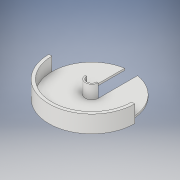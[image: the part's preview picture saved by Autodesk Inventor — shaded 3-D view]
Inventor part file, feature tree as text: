
AUTODESK INVENTOR PART (.ipt)
format: ipt  version: 2017 (Build 210142000, 142)  size: 180,736 bytes
history: native  units: in
note: dims shown in document units (in); Inventor stores cm internally (conversion verified against a paired STEP export)
features: sketch x10, extrude x9, projected_geometry x1
ambient origin geometry x8: Origin, YZ Plane, XZ Plane, XY Plane, X Axis, Y Axis, Z Axis, Center Point
bodies: Solid1 (feature_tree)
feature tree (20):
  extrude  "Extrusion1"  Depth=1.1024in TaperAngle=0.0deg
  extrude  "Extrusion2"  Depth=0.6496in TaperAngle=0.0deg
  extrude  "Extrusion3"  Depth=0.8268in
  extrude  "Extrusion4"  Depth=0.8661in TaperAngle=0.0deg
  extrude  "Extrusion5"  Depth=0.1181in TaperAngle=0.0deg
  extrude  "Extrusion6"  Depth=0.1181in TaperAngle=0.0deg
  sketch  "Sketch7"  dims[d22=0.1181in d23=0.0in]
  extrude  "Extrusion7"  [1 undecoded]
  extrude  "Extrusion8"  [1 undecoded]
  extrude  "Extrusion9"  [1 undecoded]
  sketch  "Sketch1"  dims[d0=5.5118in d1=1.1024in d2=0.0in]
  sketch  "Sketch2"  dims[d3=0.6496in d4=11.0236in d5=0.0in]
  sketch  "Sketch3"  dims[d6=5.1181in d7=0.8268in]
  sketch  "Sketch4"  dims[d8=0.8661in d9=0.0in d10=8.6614in d11=0.0in]
  sketch  "Sketch5"  dims[d12=0.1181in d13=0.0in d14=0.1181in d15=0.0in]
  sketch  "Sketch6"  dims[d16=0.1181in d17=0.0in d18=1.1811in d19=0.0in]
  projected_geometry  "Projected Loop1"
  sketch  "Sketch8"
  sketch  "Sketch9"
  sketch  "Sketch10"
note: 3 required parameter values undecoded (feature->parameter linkage not recoverable at this tier; creation-order binding heuristic only, values carry confidence <= 0.55)
